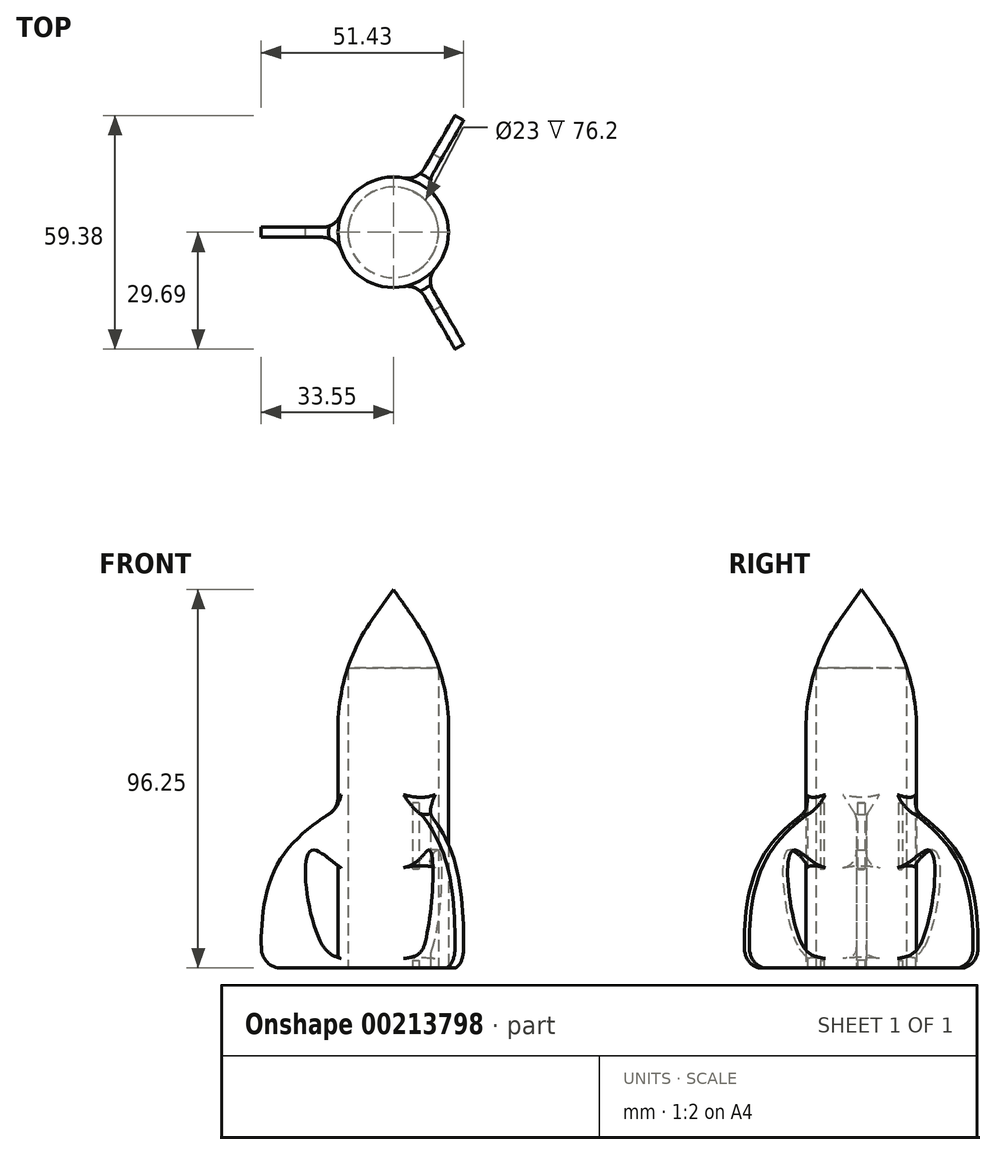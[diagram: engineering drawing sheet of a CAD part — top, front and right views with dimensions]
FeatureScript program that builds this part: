
annotation { "Feature Type Name" : "Feature", "Feature Type Description" : "" }
export const myFeature = defineFeature(function(context is Context, id is Id, definition is map)
    precondition{}
    {
        {
            var Q0;
            Q0=qCreatedBy(makeId("Top.planeOp"),FACE);
            var sketch = newSketch(context, id + "F0", { "sketchPlane" : qUnion([Q0])});
            skCircle(sketch, "E0", {"center": v(0, 0) * mm, "radius": 11.5 * mm});
            skCircle(sketch, "E1", {"center": v(0, 0) * mm, "radius": 14.04 * mm});
            skSolve(sketch);
        }
        {
            var Q0;
            Q0=makeQuery(id+"F0.imprint","IMPRINT",FACE,{"disambiguationData":[TD([[makeQuery(id+"F0.imprint","IMPRINT",EDGE,{"derivedFrom":sQuery(id+"F0.wireOp",EDGE,"E0")}),-1.0]])]});
            extrude(context, id + "F1", {"entities" : qUnion([Q0]), "depth" : 76.2 * mm});
        }
        {
            var Q0;
            Q0=qCreatedBy(makeId("Top.planeOp"),FACE);
            cPlane(context, id + "F2", {"entities" : qUnion([Q0]), "cplaneType" : CPlaneType.OFFSET, "offset" : 76.2 * mm, "width" : 152.4 * mm, "height" : 152.4 * mm});
        }
        {
            var Q0;
            Q0=qCreatedBy(id+"F2.planeOp",FACE);
            var sketch = newSketch(context, id + "F3", { "sketchPlane" : qUnion([Q0])});
            skCircle(sketch, "E2.0", {"center": v(0, 0) * mm, "radius": 14.04 * mm});
            skSolve(sketch);
        }
        {
            var Q0;
            Q0 = qSketchRegion(id + "F3", true);
            extrude(context, id + "F4", {"entities" : qUnion([Q0]), "operationType" : NewBodyOperationType.ADD, "depth" : 25.4 * mm, "hasDraft" : true, "draftAngle" : 35 * degree, "draftPullDirection" : true});
        }
        {
            var Q0;
            Q0=makeQuery(id+"F4.opExtrude","SWEPT_FACE",FACE,{"disambiguationData":[OSD([sQuery(id+"F3.wireOp",EDGE,"E2.0")])]});
            fillet(context, id + "F5", {"entities" : qUnion([Q0]), "radius" : 48.26 * mm, "tangentPropagation" : true, "allowEdgeOverflow" : false});
        }
        {
            var Q0;
            Q0=qCreatedBy(makeId("Front.planeOp"),FACE);
            var sketch = newSketch(context, id + "F6", { "sketchPlane" : qUnion([Q0])});
            skFitSpline(sketch, "E3", {"points": [v(-11.46, 41.94) * mm, v(-29.4, 26.34) * mm, v(-33.2, 0) * mm], "startDerivative": vector(-21.33, -11.42) * mm, "endDerivative": vector(2.93, -26.57) * mm});
            skLineSegment(sketch, "E4", {"start": v(-11.46, 41.94) * mm, "end": v(-11.46, 25.14) * mm});
            skFitSpline(sketch, "E5", {"points": [v(-11.46, 25.14) * mm, v(-20.59, 29.95) * mm, v(-18, 5.87) * mm, v(-11.46, 1.95) * mm], "startDerivative": vector(-19.43, -9.54) * mm, "endDerivative": vector(23.3, -8.7) * mm});
            skLineSegment(sketch, "E6", {"start": v(-11.46, 0) * mm, "end": v(-11.46, 1.95) * mm});
            skLineSegment(sketch, "E7", {"start": v(-33.2, 0) * mm, "end": v(-11.46, 0) * mm});
            skSolve(sketch);
        }
        {
            var Q0;
            Q0=makeQuery(id+"F6.imprint","IMPRINT",FACE,{"disambiguationData":[TD([[makeQuery(id+"F6.imprint","IMPRINT",EDGE,{"derivedFrom":sQuery(id+"F6.wireOp",EDGE,"E3")}),1.0]])]});
            extrude(context, id + "F7", {"entities" : qUnion([Q0]), "oppositeDirection" : true, "depth" : 1.27 * mm, "hasSecondDirection" : true, "secondDirectionOppositeDirection" : false, "secondDirectionDepth" : 1.27 * mm});
        }
        {
            var Q0;
            Q0=makeQuery(id+"F7.opExtrude","SWEPT_BODY",BODY,{"disambiguationData":[OSD([sQuery(id+"F6.wireOp",EDGE,"E3"),sQuery(id+"F6.wireOp",EDGE,"E4"),sQuery(id+"F6.wireOp",EDGE,"E5"),sQuery(id+"F6.wireOp",EDGE,"E6"),sQuery(id+"F6.wireOp",EDGE,"E7")])]});
            var Q1;
            Q1=makeQuery(id+"F1.opExtrude","CAP_EDGE",EDGE,{"disambiguationData":[OSD([sQuery(id+"F0.wireOp",EDGE,"E0")])],"isStart":true});
            circularPattern(context, id + "F8", {"entities" : qUnion([Q0]), "axis" : qUnion([Q1]), "angle" : 360 * degree, "instanceCount" : 3, "equalSpace" : true});
        }
        {
            var Q0;
            Q0=makeQuery(id+"F7.opExtrude","SWEPT_BODY",BODY,{"disambiguationData":[OSD([sQuery(id+"F6.wireOp",EDGE,"E3"),sQuery(id+"F6.wireOp",EDGE,"E4"),sQuery(id+"F6.wireOp",EDGE,"E5"),sQuery(id+"F6.wireOp",EDGE,"E6"),sQuery(id+"F6.wireOp",EDGE,"E7")])]});
            var Q1;
            Q1=makeQuery(id+"F8.opPattern","COPY",BODY,{"derivedFrom":makeQuery(id+"F7.opExtrude","SWEPT_BODY",BODY,{"disambiguationData":[OSD([sQuery(id+"F6.wireOp",EDGE,"E3"),sQuery(id+"F6.wireOp",EDGE,"E4"),sQuery(id+"F6.wireOp",EDGE,"E5"),sQuery(id+"F6.wireOp",EDGE,"E6"),sQuery(id+"F6.wireOp",EDGE,"E7")])]}),"instanceName":"1"});
            var Q2;
            Q2=makeQuery(id+"F1.opExtrude","SWEPT_BODY",BODY,{"disambiguationData":[OSD([sQuery(id+"F0.wireOp",EDGE,"E0"),sQuery(id+"F0.wireOp",EDGE,"E1")])]});
            var Q3;
            Q3=makeQuery(id+"F8.opPattern","COPY",BODY,{"derivedFrom":makeQuery(id+"F7.opExtrude","SWEPT_BODY",BODY,{"disambiguationData":[OSD([sQuery(id+"F6.wireOp",EDGE,"E3"),sQuery(id+"F6.wireOp",EDGE,"E4"),sQuery(id+"F6.wireOp",EDGE,"E5"),sQuery(id+"F6.wireOp",EDGE,"E6"),sQuery(id+"F6.wireOp",EDGE,"E7")])]}),"instanceName":"2"});
            booleanBodies(context, id + "F9", {"operationType" : BooleanOperationType.UNION, "tools" : qUnion([Q0, Q1, Q2, Q3])});
        }
        {
            var Q0;
            Q0=makeQuery(id+"F9.opBoolean","INTERSECT",EDGE,{"disambiguationData":[OD(1.0)],"derivedFrom":[makeQuery(id+"F1.opExtrude","SWEPT_FACE",FACE,{"disambiguationData":[OSD([sQuery(id+"F0.wireOp",EDGE,"E1")])]}),makeQuery(id+"F8.opPattern","COPY",FACE,{"derivedFrom":makeQuery(id+"F7.opExtrude","CAP_FACE",FACE,{"disambiguationData":[OSD([sQuery(id+"F6.wireOp",EDGE,"E3"),sQuery(id+"F6.wireOp",EDGE,"E4"),sQuery(id+"F6.wireOp",EDGE,"E5"),sQuery(id+"F6.wireOp",EDGE,"E6"),sQuery(id+"F6.wireOp",EDGE,"E7")])],"isStart":true}),"instanceName":"1"})]});
            var Q1;
            Q1=makeQuery(id+"F9.opBoolean","INTERSECT",EDGE,{"disambiguationData":[OD(0.0)],"derivedFrom":[makeQuery(id+"F1.opExtrude","SWEPT_FACE",FACE,{"disambiguationData":[OSD([sQuery(id+"F0.wireOp",EDGE,"E1")])]}),makeQuery(id+"F8.opPattern","COPY",FACE,{"derivedFrom":makeQuery(id+"F7.opExtrude","CAP_FACE",FACE,{"disambiguationData":[OSD([sQuery(id+"F6.wireOp",EDGE,"E3"),sQuery(id+"F6.wireOp",EDGE,"E4"),sQuery(id+"F6.wireOp",EDGE,"E5"),sQuery(id+"F6.wireOp",EDGE,"E6"),sQuery(id+"F6.wireOp",EDGE,"E7")])],"isStart":true}),"instanceName":"1"})]});
            var Q2;
            Q2=makeQuery(id+"F9.opBoolean","INTERSECT",EDGE,{"disambiguationData":[OD(1.0)],"derivedFrom":[makeQuery(id+"F1.opExtrude","SWEPT_FACE",FACE,{"disambiguationData":[OSD([sQuery(id+"F0.wireOp",EDGE,"E1")])]}),makeQuery(id+"F8.opPattern","COPY",FACE,{"derivedFrom":makeQuery(id+"F7.opExtrude","CAP_FACE",FACE,{"disambiguationData":[OSD([sQuery(id+"F6.wireOp",EDGE,"E3"),sQuery(id+"F6.wireOp",EDGE,"E4"),sQuery(id+"F6.wireOp",EDGE,"E5"),sQuery(id+"F6.wireOp",EDGE,"E6"),sQuery(id+"F6.wireOp",EDGE,"E7")])],"isStart":false}),"instanceName":"2"})]});
            var Q3;
            Q3=makeQuery(id+"F9.opBoolean","INTERSECT",EDGE,{"disambiguationData":[OD(0.0)],"derivedFrom":[makeQuery(id+"F1.opExtrude","SWEPT_FACE",FACE,{"disambiguationData":[OSD([sQuery(id+"F0.wireOp",EDGE,"E1")])]}),makeQuery(id+"F8.opPattern","COPY",FACE,{"derivedFrom":makeQuery(id+"F7.opExtrude","CAP_FACE",FACE,{"disambiguationData":[OSD([sQuery(id+"F6.wireOp",EDGE,"E3"),sQuery(id+"F6.wireOp",EDGE,"E4"),sQuery(id+"F6.wireOp",EDGE,"E5"),sQuery(id+"F6.wireOp",EDGE,"E6"),sQuery(id+"F6.wireOp",EDGE,"E7")])],"isStart":false}),"instanceName":"2"})]});
            var Q4;
            Q4=makeQuery(id+"F9.opBoolean","INTERSECT",EDGE,{"disambiguationData":[OD(1.0)],"derivedFrom":[makeQuery(id+"F1.opExtrude","SWEPT_FACE",FACE,{"disambiguationData":[OSD([sQuery(id+"F0.wireOp",EDGE,"E1")])]}),makeQuery(id+"F8.opPattern","COPY",FACE,{"derivedFrom":makeQuery(id+"F7.opExtrude","CAP_FACE",FACE,{"disambiguationData":[OSD([sQuery(id+"F6.wireOp",EDGE,"E3"),sQuery(id+"F6.wireOp",EDGE,"E4"),sQuery(id+"F6.wireOp",EDGE,"E5"),sQuery(id+"F6.wireOp",EDGE,"E6"),sQuery(id+"F6.wireOp",EDGE,"E7")])],"isStart":false}),"instanceName":"1"})]});
            var Q5;
            Q5=makeQuery(id+"F9.opBoolean","INTERSECT",EDGE,{"disambiguationData":[OD(0.0)],"derivedFrom":[makeQuery(id+"F1.opExtrude","SWEPT_FACE",FACE,{"disambiguationData":[OSD([sQuery(id+"F0.wireOp",EDGE,"E1")])]}),makeQuery(id+"F8.opPattern","COPY",FACE,{"derivedFrom":makeQuery(id+"F7.opExtrude","CAP_FACE",FACE,{"disambiguationData":[OSD([sQuery(id+"F6.wireOp",EDGE,"E3"),sQuery(id+"F6.wireOp",EDGE,"E4"),sQuery(id+"F6.wireOp",EDGE,"E5"),sQuery(id+"F6.wireOp",EDGE,"E6"),sQuery(id+"F6.wireOp",EDGE,"E7")])],"isStart":false}),"instanceName":"1"})]});
            var Q6;
            Q6=makeQuery(id+"F9.opBoolean","INTERSECT",EDGE,{"disambiguationData":[OD(1.0)],"derivedFrom":[makeQuery(id+"F1.opExtrude","SWEPT_FACE",FACE,{"disambiguationData":[OSD([sQuery(id+"F0.wireOp",EDGE,"E1")])]}),makeQuery(id+"F8.opPattern","COPY",FACE,{"derivedFrom":makeQuery(id+"F7.opExtrude","CAP_FACE",FACE,{"disambiguationData":[OSD([sQuery(id+"F6.wireOp",EDGE,"E3"),sQuery(id+"F6.wireOp",EDGE,"E4"),sQuery(id+"F6.wireOp",EDGE,"E5"),sQuery(id+"F6.wireOp",EDGE,"E6"),sQuery(id+"F6.wireOp",EDGE,"E7")])],"isStart":true}),"instanceName":"2"})]});
            var Q7;
            Q7=makeQuery(id+"F9.opBoolean","INTERSECT",EDGE,{"disambiguationData":[OD(0.0)],"derivedFrom":[makeQuery(id+"F1.opExtrude","SWEPT_FACE",FACE,{"disambiguationData":[OSD([sQuery(id+"F0.wireOp",EDGE,"E1")])]}),makeQuery(id+"F8.opPattern","COPY",FACE,{"derivedFrom":makeQuery(id+"F7.opExtrude","CAP_FACE",FACE,{"disambiguationData":[OSD([sQuery(id+"F6.wireOp",EDGE,"E3"),sQuery(id+"F6.wireOp",EDGE,"E4"),sQuery(id+"F6.wireOp",EDGE,"E5"),sQuery(id+"F6.wireOp",EDGE,"E6"),sQuery(id+"F6.wireOp",EDGE,"E7")])],"isStart":true}),"instanceName":"2"})]});
            var Q8;
            Q8=makeQuery(id+"F9.opBoolean","INTERSECT",EDGE,{"disambiguationData":[OD(1.0)],"derivedFrom":[makeQuery(id+"F1.opExtrude","SWEPT_FACE",FACE,{"disambiguationData":[OSD([sQuery(id+"F0.wireOp",EDGE,"E1")])]}),makeQuery(id+"F7.opExtrude","CAP_FACE",FACE,{"disambiguationData":[OSD([sQuery(id+"F6.wireOp",EDGE,"E3"),sQuery(id+"F6.wireOp",EDGE,"E4"),sQuery(id+"F6.wireOp",EDGE,"E5"),sQuery(id+"F6.wireOp",EDGE,"E6"),sQuery(id+"F6.wireOp",EDGE,"E7")])],"isStart":false})]});
            var Q9;
            Q9=makeQuery(id+"F9.opBoolean","INTERSECT",EDGE,{"disambiguationData":[OD(0.0)],"derivedFrom":[makeQuery(id+"F1.opExtrude","SWEPT_FACE",FACE,{"disambiguationData":[OSD([sQuery(id+"F0.wireOp",EDGE,"E1")])]}),makeQuery(id+"F7.opExtrude","CAP_FACE",FACE,{"disambiguationData":[OSD([sQuery(id+"F6.wireOp",EDGE,"E3"),sQuery(id+"F6.wireOp",EDGE,"E4"),sQuery(id+"F6.wireOp",EDGE,"E5"),sQuery(id+"F6.wireOp",EDGE,"E6"),sQuery(id+"F6.wireOp",EDGE,"E7")])],"isStart":false})]});
            var Q10;
            Q10=makeQuery(id+"F9.opBoolean","INTERSECT",EDGE,{"disambiguationData":[OD(1.0)],"derivedFrom":[makeQuery(id+"F1.opExtrude","SWEPT_FACE",FACE,{"disambiguationData":[OSD([sQuery(id+"F0.wireOp",EDGE,"E1")])]}),makeQuery(id+"F7.opExtrude","CAP_FACE",FACE,{"disambiguationData":[OSD([sQuery(id+"F6.wireOp",EDGE,"E3"),sQuery(id+"F6.wireOp",EDGE,"E4"),sQuery(id+"F6.wireOp",EDGE,"E5"),sQuery(id+"F6.wireOp",EDGE,"E6"),sQuery(id+"F6.wireOp",EDGE,"E7")])],"isStart":true})]});
            var Q11;
            Q11=makeQuery(id+"F9.opBoolean","INTERSECT",EDGE,{"disambiguationData":[OD(0.0)],"derivedFrom":[makeQuery(id+"F1.opExtrude","SWEPT_FACE",FACE,{"disambiguationData":[OSD([sQuery(id+"F0.wireOp",EDGE,"E1")])]}),makeQuery(id+"F7.opExtrude","CAP_FACE",FACE,{"disambiguationData":[OSD([sQuery(id+"F6.wireOp",EDGE,"E3"),sQuery(id+"F6.wireOp",EDGE,"E4"),sQuery(id+"F6.wireOp",EDGE,"E5"),sQuery(id+"F6.wireOp",EDGE,"E6"),sQuery(id+"F6.wireOp",EDGE,"E7")])],"isStart":true})]});
            fillet(context, id + "F10", {"entities" : qUnion([Q0, Q1, Q2, Q3, Q4, Q5, Q6, Q7, Q8, Q9, Q10, Q11]), "radius" : 5.08 * mm, "tangentPropagation" : true, "allowEdgeOverflow" : false});
        }
        {
            var Q0;
            Q0=makeQuery(id+"F9.opBoolean","INTERSECT",EDGE,{"derivedFrom":[makeQuery(id+"F1.opExtrude","SWEPT_FACE",FACE,{"disambiguationData":[OSD([sQuery(id+"F0.wireOp",EDGE,"E1")])]}),makeQuery(id+"F7.opExtrude","SWEPT_FACE",FACE,{"disambiguationData":[OSD([sQuery(id+"F6.wireOp",EDGE,"E3")])]})]});
            var Q1;
            Q1=makeQuery(id+"F9.opBoolean","INTERSECT",EDGE,{"derivedFrom":[makeQuery(id+"F1.opExtrude","SWEPT_FACE",FACE,{"disambiguationData":[OSD([sQuery(id+"F0.wireOp",EDGE,"E1")])]}),makeQuery(id+"F8.opPattern","COPY",FACE,{"derivedFrom":makeQuery(id+"F7.opExtrude","SWEPT_FACE",FACE,{"disambiguationData":[OSD([sQuery(id+"F6.wireOp",EDGE,"E3")])]}),"instanceName":"1"})]});
            var Q2;
            Q2=makeQuery(id+"F9.opBoolean","INTERSECT",EDGE,{"derivedFrom":[makeQuery(id+"F1.opExtrude","SWEPT_FACE",FACE,{"disambiguationData":[OSD([sQuery(id+"F0.wireOp",EDGE,"E1")])]}),makeQuery(id+"F8.opPattern","COPY",FACE,{"derivedFrom":makeQuery(id+"F7.opExtrude","SWEPT_FACE",FACE,{"disambiguationData":[OSD([sQuery(id+"F6.wireOp",EDGE,"E3")])]}),"instanceName":"2"})]});
            fillet(context, id + "F11", {"entities" : qUnion([Q0, Q1, Q2]), "radius" : 5.08 * mm, "tangentPropagation" : true, "allowEdgeOverflow" : false});
        }
        {
            var Q0;
            Q0=makeQuery(id+"F7.opExtrude","SWEPT_EDGE",EDGE,{"disambiguationData":[OSD([sQuery(id+"F6.wireOp",EDGE,"E3"),sQuery(id+"F6.wireOp",EDGE,"E7")])]});
            var Q1;
            Q1=makeQuery(id+"F8.opPattern","COPY",EDGE,{"derivedFrom":makeQuery(id+"F7.opExtrude","SWEPT_EDGE",EDGE,{"disambiguationData":[OSD([sQuery(id+"F6.wireOp",EDGE,"E3"),sQuery(id+"F6.wireOp",EDGE,"E7")])]}),"instanceName":"2"});
            var Q2;
            Q2=makeQuery(id+"F8.opPattern","COPY",EDGE,{"derivedFrom":makeQuery(id+"F7.opExtrude","SWEPT_EDGE",EDGE,{"disambiguationData":[OSD([sQuery(id+"F6.wireOp",EDGE,"E3"),sQuery(id+"F6.wireOp",EDGE,"E7")])]}),"instanceName":"1"});
            fillet(context, id + "F12", {"entities" : qUnion([Q0, Q1, Q2]), "radius" : 5.08 * mm, "tangentPropagation" : true, "allowEdgeOverflow" : false});
        }
    });
